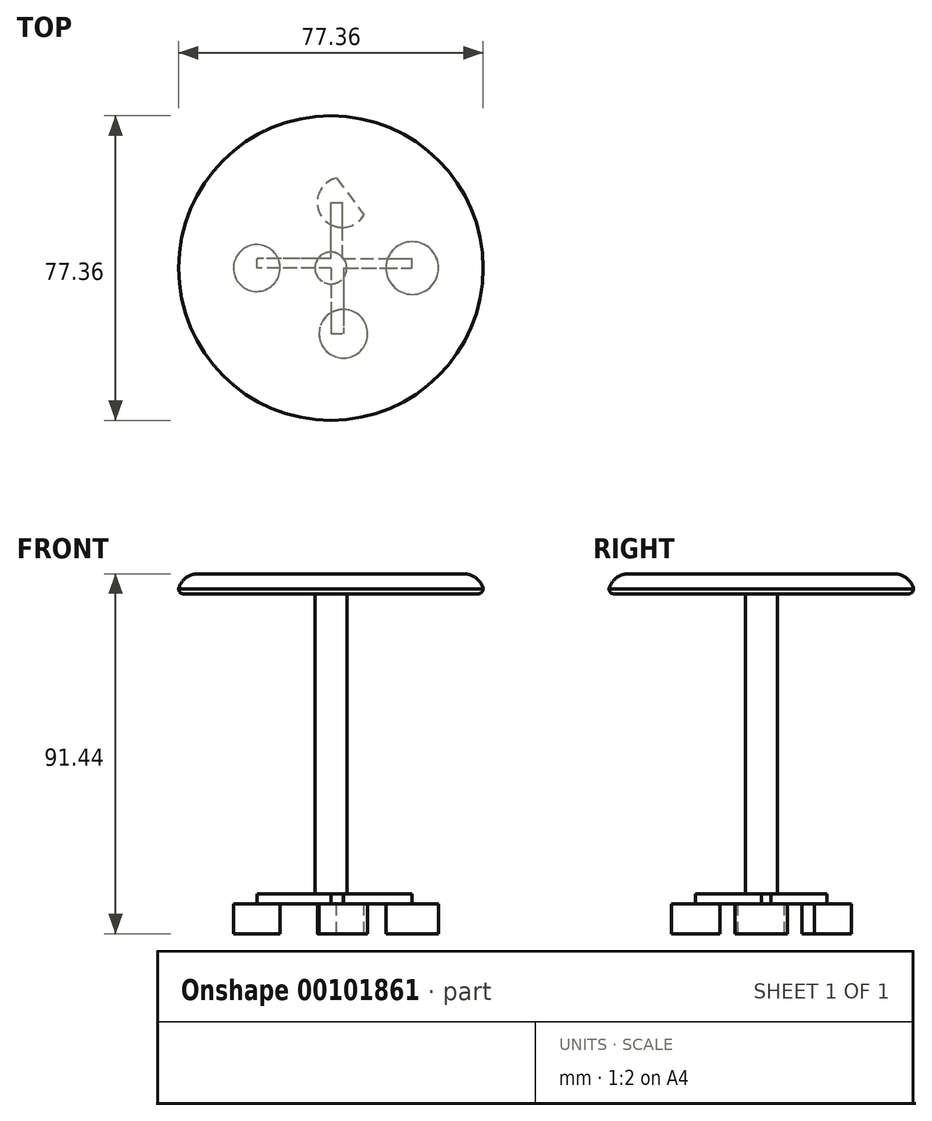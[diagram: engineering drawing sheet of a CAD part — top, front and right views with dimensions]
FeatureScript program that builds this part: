
annotation { "Feature Type Name" : "Feature", "Feature Type Description" : "" }
export const myFeature = defineFeature(function(context is Context, id is Id, definition is map)
    precondition{}
    {
        {
            var Q0;
            Q0=qCreatedBy(makeId("Top.planeOp"),FACE);
            var sketch = newSketch(context, id + "F0", { "sketchPlane" : qUnion([Q0])});
            skCircle(sketch, "E0", {"center": v(0, 0) * mm, "radius": 38.68 * mm});
            skSolve(sketch);
        }
        {
            var Q0;
            Q0 = qSketchRegion(id + "F0", true);
            extrude(context, id + "F1", {"entities" : qUnion([Q0]), "depth" : 5.08 * mm});
        }
        {
            var Q0;
            Q0=makeQuery(id+"F1.opExtrude","CAP_FACE",FACE,{"disambiguationData":[OSD([sQuery(id+"F0.wireOp",EDGE,"E0")])],"isStart":true});
            var sketch = newSketch(context, id + "F2", { "sketchPlane" : qUnion([Q0])});
            skCircle(sketch, "E1", {"center": v(0, 0) * mm, "radius": 4.05 * mm});
            skSolve(sketch);
        }
        {
            var Q0;
            Q0 = qSketchRegion(id + "F2", true);
            extrude(context, id + "F3", {"entities" : qUnion([Q0]), "operationType" : NewBodyOperationType.ADD, "depth" : 76.2 * mm});
        }
        {
            var Q0;
            Q0=makeQuery(id+"F3.opExtrude","CAP_FACE",FACE,{"disambiguationData":[OSD([sQuery(id+"F2.wireOp",EDGE,"E1")])],"isStart":false});
            var sketch = newSketch(context, id + "F4", { "sketchPlane" : qUnion([Q0])});
            skLineSegment(sketch, "E2.bottom", {"start": v(0, 0) * mm, "end": v(20.66, 0) * mm});
            skLineSegment(sketch, "E2.top", {"start": v(0, -2.39) * mm, "end": v(20.66, -2.39) * mm});
            skLineSegment(sketch, "E2.left", {"start": v(0, 0) * mm, "end": v(0, -2.39) * mm});
            skLineSegment(sketch, "E2.right", {"start": v(20.66, 0) * mm, "end": v(20.66, -2.39) * mm});
            skLineSegment(sketch, "E3.bottom", {"start": v(0, 0) * mm, "end": v(3.18, 0) * mm});
            skLineSegment(sketch, "E3.top", {"start": v(0, 16.69) * mm, "end": v(3.18, 16.69) * mm});
            skLineSegment(sketch, "E3.left", {"start": v(0, 0) * mm, "end": v(0, 16.69) * mm});
            skLineSegment(sketch, "E3.right", {"start": v(3.18, 0) * mm, "end": v(3.18, 16.69) * mm});
            skLineSegment(sketch, "E4.bottom", {"start": v(0, 0) * mm, "end": v(-18.81, 0) * mm});
            skLineSegment(sketch, "E4.top", {"start": v(0, -2.39) * mm, "end": v(-18.81, -2.39) * mm});
            skLineSegment(sketch, "E4.right", {"start": v(-18.81, 0) * mm, "end": v(-18.81, -2.39) * mm});
            skLineSegment(sketch, "E5.bottom", {"start": v(0, -2.39) * mm, "end": v(2.91, -2.39) * mm});
            skLineSegment(sketch, "E5.top", {"start": v(0, -16.7) * mm, "end": v(2.91, -16.7) * mm});
            skLineSegment(sketch, "E5.left", {"start": v(0, -2.39) * mm, "end": v(0, -16.7) * mm});
            skLineSegment(sketch, "E5.right", {"start": v(2.91, -2.39) * mm, "end": v(2.91, -16.7) * mm});
            skSolve(sketch);
        }
        {
            var Q0;
            Q0 = qSketchRegion(id + "F4", true);
            extrude(context, id + "F5", {"entities" : qUnion([Q0]), "operationType" : NewBodyOperationType.ADD, "depth" : 2.54 * mm});
        }
        {
            var Q0;
            Q0=makeQuery(id+"F1.opExtrude","CAP_EDGE",EDGE,{"disambiguationData":[OSD([sQuery(id+"F0.wireOp",EDGE,"E0")])],"isStart":true});
            fillet(context, id + "F6", {"entities" : qUnion([Q0]), "radius" : 1.27 * mm, "tangentPropagation" : true, "allowEdgeOverflow" : false});
        }
        {
            var Q0;
            Q0=makeQuery(id+"F1.opExtrude","CAP_EDGE",EDGE,{"disambiguationData":[OSD([sQuery(id+"F0.wireOp",EDGE,"E0")])],"isStart":false});
            fillet(context, id + "F7", {"entities" : qUnion([Q0]), "radius" : 5.08 * mm, "tangentPropagation" : true, "allowEdgeOverflow" : false});
        }
        {
            var Q0;
            Q0=makeQuery(id+"F5.opExtrude","CAP_FACE",FACE,{"disambiguationData":[OSD([sQuery(id+"F4.wireOp",EDGE,"E2.bottom"),sQuery(id+"F4.wireOp",EDGE,"E2.top"),sQuery(id+"F4.wireOp",EDGE,"E2.right"),sQuery(id+"F4.wireOp",EDGE,"E3.top"),sQuery(id+"F4.wireOp",EDGE,"E3.left"),sQuery(id+"F4.wireOp",EDGE,"E3.right"),sQuery(id+"F4.wireOp",EDGE,"E4.bottom"),sQuery(id+"F4.wireOp",EDGE,"E4.top"),sQuery(id+"F4.wireOp",EDGE,"E4.right"),sQuery(id+"F4.wireOp",EDGE,"E5.top"),sQuery(id+"F4.wireOp",EDGE,"E5.left"),sQuery(id+"F4.wireOp",EDGE,"E5.right")])],"isStart":false});
            var sketch = newSketch(context, id + "F8", { "sketchPlane" : qUnion([Q0])});
            skCircle(sketch, "E6", {"center": v(20.66, 0) * mm, "radius": 6.69 * mm});
            skCircle(sketch, "E7", {"center": v(-18.81, 0) * mm, "radius": 5.93 * mm});
            skCircle(sketch, "E8", {"center": v(2.91, -16.7) * mm, "radius": 6.36 * mm});
            skCircle(sketch, "E9", {"center": v(3.18, 16.69) * mm, "radius": 6.16 * mm});
            skSolve(sketch);
        }
        {
            var Q0;
            Q0 = qSketchRegion(id + "F8", true);
            extrude(context, id + "F9", {"entities" : qUnion([Q0]), "operationType" : NewBodyOperationType.ADD, "depth" : 7.62 * mm});
        }
        {
            var Q0;
            Q0=makeQuery(id+"F9.opExtrude","CAP_FACE",FACE,{"disambiguationData":[OSD([sQuery(id+"F8.wireOp",EDGE,"E8")])],"isStart":true});
            var sketch = newSketch(context, id + "F10", { "sketchPlane" : qUnion([Q0])});
            skLineSegment(sketch, "E10", {"start": v(8.42, 13.5) * mm, "end": v(1.41, 22.88) * mm});
            skPoint(sketch, "E10.endSnap0", {"position": v(4.41, 22.88) * mm});
            skLineSegment(sketch, "E11", {"start": v(1.41, 22.88) * mm, "end": v(10.41, 29.6) * mm});
            skLineSegment(sketch, "E12", {"start": v(10.41, 29.6) * mm, "end": v(18.21, 35.66) * mm});
            skLineSegment(sketch, "E13", {"start": v(18.21, 35.66) * mm, "end": v(25.22, 26.64) * mm});
            skLineSegment(sketch, "E14", {"start": v(25.22, 26.64) * mm, "end": v(8.42, 13.5) * mm});
            skSolve(sketch);
        }
        {
            var Q0;
            Q0 = qSketchRegion(id + "F10", true);
            extrude(context, id + "F11", {"entities" : qUnion([Q0]), "operationType" : NewBodyOperationType.REMOVE, "endBound" : BoundingType.THROUGH_ALL, "oppositeDirection" : true, "depth" : 25.4 * mm});
        }
    });
